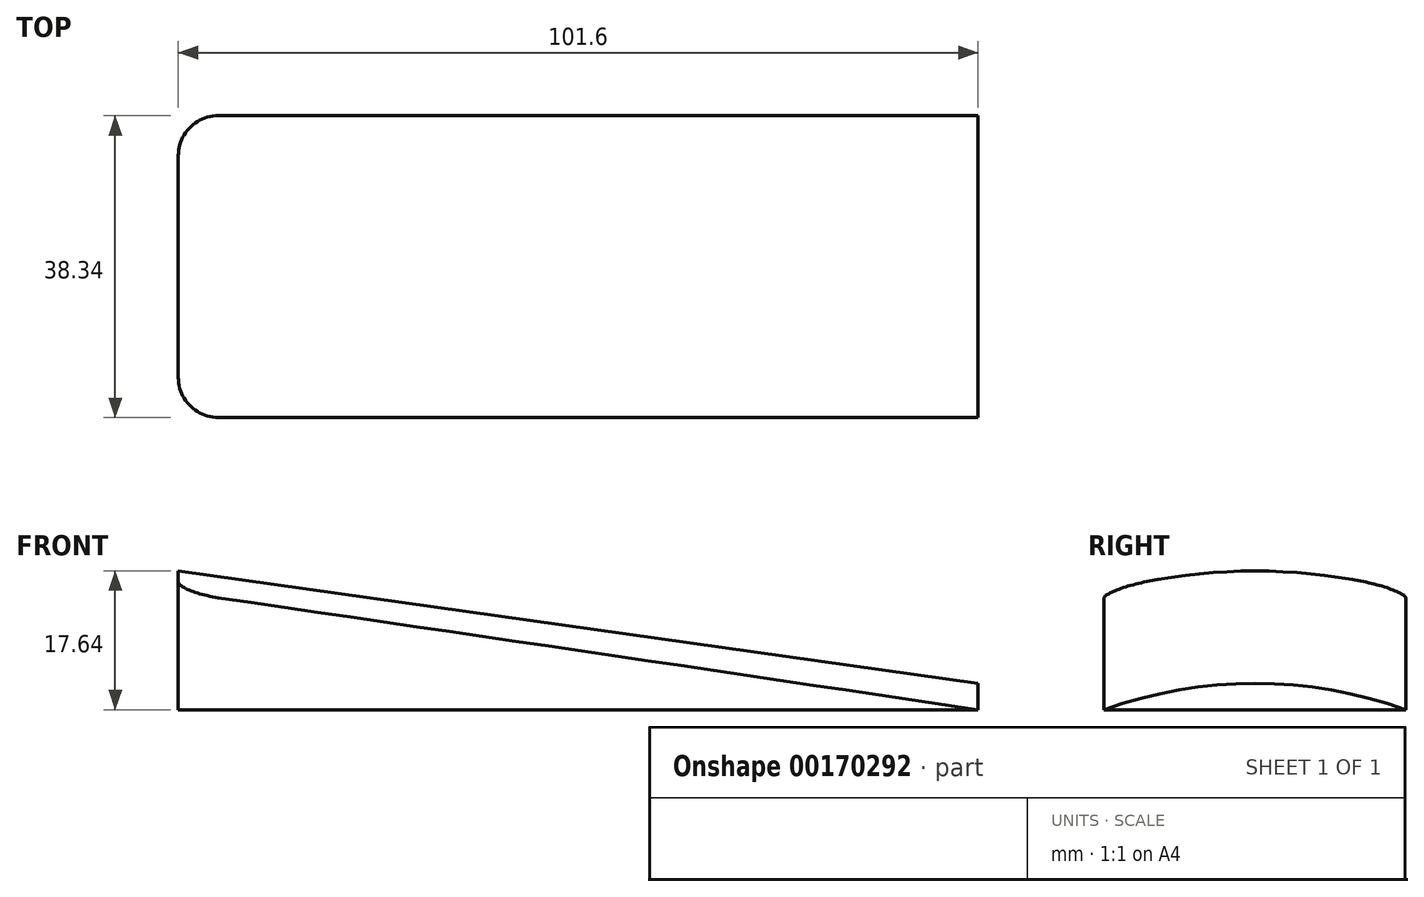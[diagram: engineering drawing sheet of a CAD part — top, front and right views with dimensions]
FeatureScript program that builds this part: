
annotation { "Feature Type Name" : "Feature", "Feature Type Description" : "" }
export const myFeature = defineFeature(function(context is Context, id is Id, definition is map)
    precondition{}
    {
        {
            var Q0;
            Q0=qCreatedBy(makeId("Right.planeOp"),FACE);
            var sketch = newSketch(context, id + "F0", { "sketchPlane" : qUnion([Q0])});
            skArc(sketch, "E0", {"start": v(47.44, 30.48) * mm, "mid": v(0, 56.39) * mm, "end": v(-47.44, 30.48) * mm});
            skLineSegment(sketch, "E1", {"start": v(-47.44, 30.48) * mm, "end": v(47.44, 30.48) * mm});
            skSolve(sketch);
        }
        {
            var Q0;
            Q0=qCreatedBy(makeId("Right.planeOp"),FACE);
            cPlane(context, id + "F1", {"entities" : qUnion([Q0]), "cplaneType" : CPlaneType.OFFSET, "offset" : 17.9 * mm, "oppositeDirection" : true, "width" : 152.4 * mm, "height" : 152.4 * mm});
        }
        {
            var Q0;
            Q0=qCreatedBy(id+"F1.planeOp",FACE);
            var sketch = newSketch(context, id + "F2", { "sketchPlane" : qUnion([Q0])});
            skArc(sketch, "E2", {"start": v(50.3, 30.48) * mm, "mid": v(0, 58.81) * mm, "end": v(-50.3, 30.48) * mm});
            skLineSegment(sketch, "E3", {"start": v(-50.3, 30.48) * mm, "end": v(50.3, 30.48) * mm});
            skSolve(sketch);
        }
        {
            var Q0;
            Q0=sQuery(id+"F2.wireOp",EDGE,"E3");
            cPlane(context, id + "F3", {"entities" : qUnion([Q0]), "cplaneType" : CPlaneType.LINE_ANGLE, "offset" : 25.4 * mm, "angle" : 0 * degree, "width" : 152.4 * mm, "height" : 152.4 * mm});
        }
        {
            var Q0;
            Q0 = qSketchRegion(id + "F0", true);
            extrude(context, id + "F4", {"entities" : qUnion([Q0]), "oppositeDirection" : true, "depth" : 101.6 * mm, "hasDraft" : true, "draftAngle" : 8 * degree});
        }
        {
            var Q0;
            Q0=makeQuery(id+"F4.opExtrude","CAP_FACE",FACE,{"disambiguationData":[OSD([sQuery(id+"F0.wireOp",EDGE,"E0"),sQuery(id+"F0.wireOp",EDGE,"E1")])],"isStart":false});
            var sketch = newSketch(context, id + "F5", { "sketchPlane" : qUnion([Q0])});
            skLineSegment(sketch, "E4.bottom", {"start": v(179.47, -23.12) * mm, "end": v(-203.83, -23.12) * mm});
            skLineSegment(sketch, "E4.top", {"start": v(179.47, 53.03) * mm, "end": v(-203.83, 53.03) * mm});
            skLineSegment(sketch, "E4.left", {"start": v(179.47, -23.12) * mm, "end": v(179.47, 53.03) * mm});
            skLineSegment(sketch, "E4.right", {"start": v(-203.83, -23.12) * mm, "end": v(-203.83, 53.03) * mm});
            skSolve(sketch);
        }
        {
            var Q0;
            {var subQ4=makeQuery(id+"F4.opExtrude","CAP_EDGE",EDGE,{"disambiguationData":[OSD([sQuery(id+"F0.wireOp",EDGE,"E1")])],"isStart":false});Q0=makeQuery(id+"F5.imprint","IMPRINT",FACE,{"disambiguationData":[TD([[makeQuery(id+"F5.imprint","IMPRINT",EDGE,{"derivedFrom":subQ4}),-1.0]])]});}
            extrude(context, id + "F6", {"entities" : qUnion([Q0]), "operationType" : NewBodyOperationType.REMOVE, "endBound" : BoundingType.THROUGH_ALL, "oppositeDirection" : true, "depth" : 127 * mm});
        }
        {
            var Q0;
            Q0=makeQuery(id+"F0.imprint","IMPRINT",FACE,{"disambiguationData":[TD([[makeQuery(id+"F0.imprint","IMPRINT",EDGE,{"derivedFrom":sQuery(id+"F0.wireOp",EDGE,"E0")}),1.0]])]});
            var sketch = newSketch(context, id + "F7", { "sketchPlane" : qUnion([Q0])});
            skLineSegment(sketch, "E5.bottom", {"start": v(-19.17, 53.03) * mm, "end": v(-54.1, 53.03) * mm});
            skLineSegment(sketch, "E5.top", {"start": v(-19.17, 91.13) * mm, "end": v(-54.1, 91.13) * mm});
            skLineSegment(sketch, "E5.left", {"start": v(-19.17, 53.03) * mm, "end": v(-19.17, 91.13) * mm});
            skLineSegment(sketch, "E5.right", {"start": v(-54.1, 53.03) * mm, "end": v(-54.1, 91.13) * mm});
            skLineSegment(sketch, "E6.bottom", {"start": v(19.17, 53.03) * mm, "end": v(54.1, 53.03) * mm});
            skLineSegment(sketch, "E6.top", {"start": v(19.17, 91.13) * mm, "end": v(54.1, 91.13) * mm});
            skLineSegment(sketch, "E6.left", {"start": v(19.17, 53.03) * mm, "end": v(19.17, 91.13) * mm});
            skLineSegment(sketch, "E6.right", {"start": v(54.1, 53.03) * mm, "end": v(54.1, 91.13) * mm});
            skSolve(sketch);
        }
        {
            var Q0;
            Q0 = qSketchRegion(id + "F7", true);
            extrude(context, id + "F8", {"entities" : qUnion([Q0]), "operationType" : NewBodyOperationType.REMOVE, "endBound" : BoundingType.THROUGH_ALL, "oppositeDirection" : true, "depth" : 25.4 * mm});
        }
        {
            var Q0;
            Q0=makeQuery(id+"F8.boolean.opBoolean","INTERSECT",EDGE,{"derivedFrom":[makeQuery(id+"F4.opExtrude","CAP_FACE",FACE,{"disambiguationData":[OSD([sQuery(id+"F0.wireOp",EDGE,"E0"),sQuery(id+"F0.wireOp",EDGE,"E1")])],"isStart":false}),makeQuery(id+"F8.opExtrude","SWEPT_FACE",FACE,{"disambiguationData":[OSD([sQuery(id+"F7.wireOp",EDGE,"E5.left")])]})]});
            var Q1;
            Q1=makeQuery(id+"F8.boolean.opBoolean","INTERSECT",EDGE,{"derivedFrom":[makeQuery(id+"F4.opExtrude","CAP_FACE",FACE,{"disambiguationData":[OSD([sQuery(id+"F0.wireOp",EDGE,"E0"),sQuery(id+"F0.wireOp",EDGE,"E1")])],"isStart":false}),makeQuery(id+"F8.opExtrude","SWEPT_FACE",FACE,{"disambiguationData":[OSD([sQuery(id+"F7.wireOp",EDGE,"E6.left")])]})]});
            var Q2;
            Q2=makeQuery(id+"F8.boolean.opBoolean","COPY",EDGE,{"derivedFrom":makeQuery(id+"F8.opExtrude","SWEPT_EDGE",EDGE,{"disambiguationData":[OSD([sQuery(id+"F0.wireOp",EDGE,"E0"),sQuery(id+"F7.wireOp",EDGE,"E6.bottom"),sQuery(id+"F7.wireOp",EDGE,"E6.left")])]})});
            var Q3;
            Q3=makeQuery(id+"F8.boolean.opBoolean","COPY",EDGE,{"derivedFrom":makeQuery(id+"F8.opExtrude","SWEPT_EDGE",EDGE,{"disambiguationData":[OSD([sQuery(id+"F0.wireOp",EDGE,"E0"),sQuery(id+"F7.wireOp",EDGE,"E5.bottom"),sQuery(id+"F7.wireOp",EDGE,"E5.left")])]})});
            var Q4;
            Q4=makeQuery(id+"F6.boolean.opBoolean","COPY",EDGE,{"derivedFrom":makeQuery(id+"F6.opExtrude","CAP_EDGE",EDGE,{"disambiguationData":[OSD([sQuery(id+"F5.wireOp",EDGE,"E4.top")])],"isStart":true})});
            fillet(context, id + "F9", {"entities" : qUnion([Q0, Q1, Q2, Q3, Q4]), "radius" : 5.08 * mm, "tangentPropagation" : true, "allowEdgeOverflow" : false});
        }
    });
